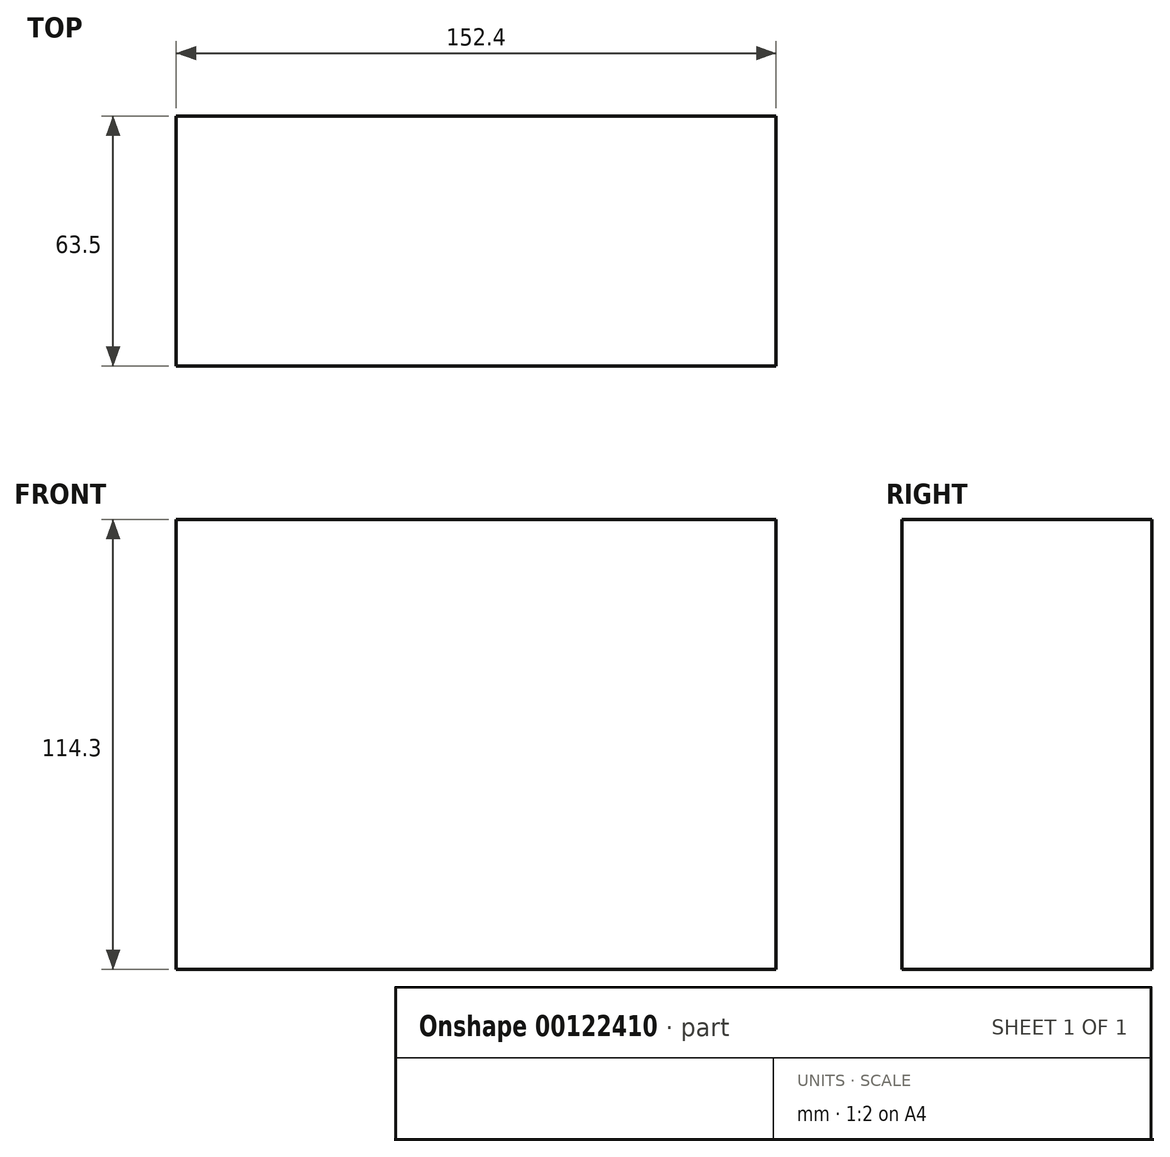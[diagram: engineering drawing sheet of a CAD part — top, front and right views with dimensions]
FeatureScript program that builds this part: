
annotation { "Feature Type Name" : "Feature", "Feature Type Description" : "" }
export const myFeature = defineFeature(function(context is Context, id is Id, definition is map)
    precondition{}
    {
        {
            var Q0;
            Q0=qCreatedBy(makeId("Top.planeOp"),FACE);
            var sketch = newSketch(context, id + "F0", { "sketchPlane" : qUnion([Q0])});
            skLineSegment(sketch, "E0.bottom", {"start": v(76.2, 31.75) * mm, "end": v(-76.2, 31.75) * mm});
            skLineSegment(sketch, "E0.top", {"start": v(76.2, -31.75) * mm, "end": v(-76.2, -31.75) * mm});
            skLineSegment(sketch, "E0.left", {"start": v(76.2, 31.75) * mm, "end": v(76.2, -31.75) * mm});
            skLineSegment(sketch, "E0.right", {"start": v(-76.2, 31.75) * mm, "end": v(-76.2, -31.75) * mm});
            skPoint(sketch, "E0.middle", {"position": v(0, 0) * mm});
            skSolve(sketch);
        }
        {
            var Q0;
            Q0 = qSketchRegion(id + "F0", true);
            extrude(context, id + "F1", {"entities" : qUnion([Q0]), "depth" : 114.3 * mm, "offsetDistance" : 25.4 * mm});
        }
    });
